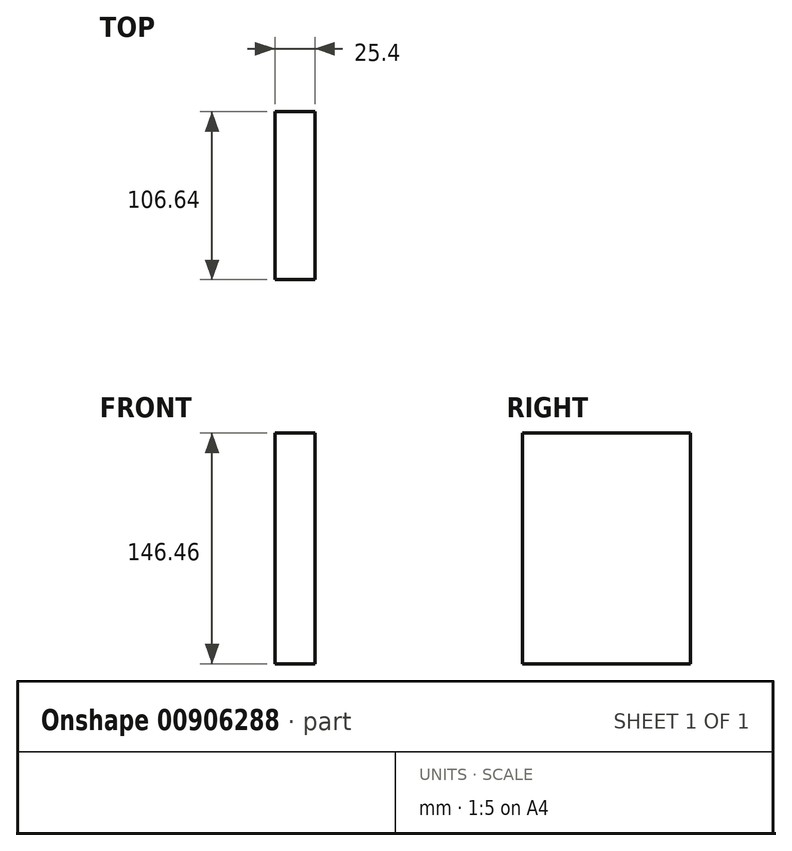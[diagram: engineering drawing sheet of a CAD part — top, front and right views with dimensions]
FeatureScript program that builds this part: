
annotation { "Feature Type Name" : "Feature", "Feature Type Description" : "" }
export const myFeature = defineFeature(function(context is Context, id is Id, definition is map)
    precondition{}
    {
        {
            var Q0;
            Q0=qCreatedBy(makeId("Right.planeOp"),FACE);
            var sketch = newSketch(context, id + "F0", { "sketchPlane" : qUnion([Q0])});
            skLineSegment(sketch, "E0.bottom", {"start": v(106.64, 146.46) * mm, "end": v(0, 146.46) * mm});
            skLineSegment(sketch, "E0.top", {"start": v(106.64, 0) * mm, "end": v(0, 0) * mm});
            skLineSegment(sketch, "E0.left", {"start": v(106.64, 146.46) * mm, "end": v(106.64, 0) * mm});
            skLineSegment(sketch, "E0.right", {"start": v(0, 146.46) * mm, "end": v(0, 0) * mm});
            skLineSegment(sketch, "E1.bottom", {"start": v(106.64, 146.46) * mm, "end": v(0, 146.46) * mm, "construction": true});
            skLineSegment(sketch, "E1.top", {"start": v(106.64, 146.46) * mm, "end": v(0, 146.46) * mm, "construction": true});
            skLineSegment(sketch, "E1.left", {"start": v(106.64, 146.46) * mm, "end": v(106.64, 146.46) * mm});
            skLineSegment(sketch, "E1.right", {"start": v(0, 146.46) * mm, "end": v(0, 146.46) * mm});
            skLineSegment(sketch, "E2.bottom", {"start": v(101.32, 213.2) * mm, "end": v(0, 213.2) * mm, "construction": true});
            skLineSegment(sketch, "E2.top", {"start": v(101.32, 206.78) * mm, "end": v(0, 206.78) * mm, "construction": true});
            skLineSegment(sketch, "E2.left", {"start": v(101.32, 213.2) * mm, "end": v(101.32, 206.78) * mm, "construction": true});
            skLineSegment(sketch, "E2.right", {"start": v(0, 213.2) * mm, "end": v(0, 206.78) * mm, "construction": true});
            skLineSegment(sketch, "E3.bottom", {"start": v(0, 0) * mm, "end": v(82.6, 0) * mm, "construction": true});
            skLineSegment(sketch, "E3.top", {"start": v(0, 146.46) * mm, "end": v(82.6, 146.46) * mm, "construction": true});
            skLineSegment(sketch, "E3.left", {"start": v(0, 0) * mm, "end": v(0, 146.46) * mm, "construction": true});
            skLineSegment(sketch, "E3.right", {"start": v(82.6, 0) * mm, "end": v(82.6, 146.46) * mm, "construction": true});
            skSolve(sketch);
        }
        {
            var Q0;
            Q0 = qSketchRegion(id + "F0", true);
            extrude(context, id + "F1", {"entities" : qUnion([Q0]), "depth" : 25.4 * mm, "offsetDistance" : 25.4 * mm});
        }
    });
